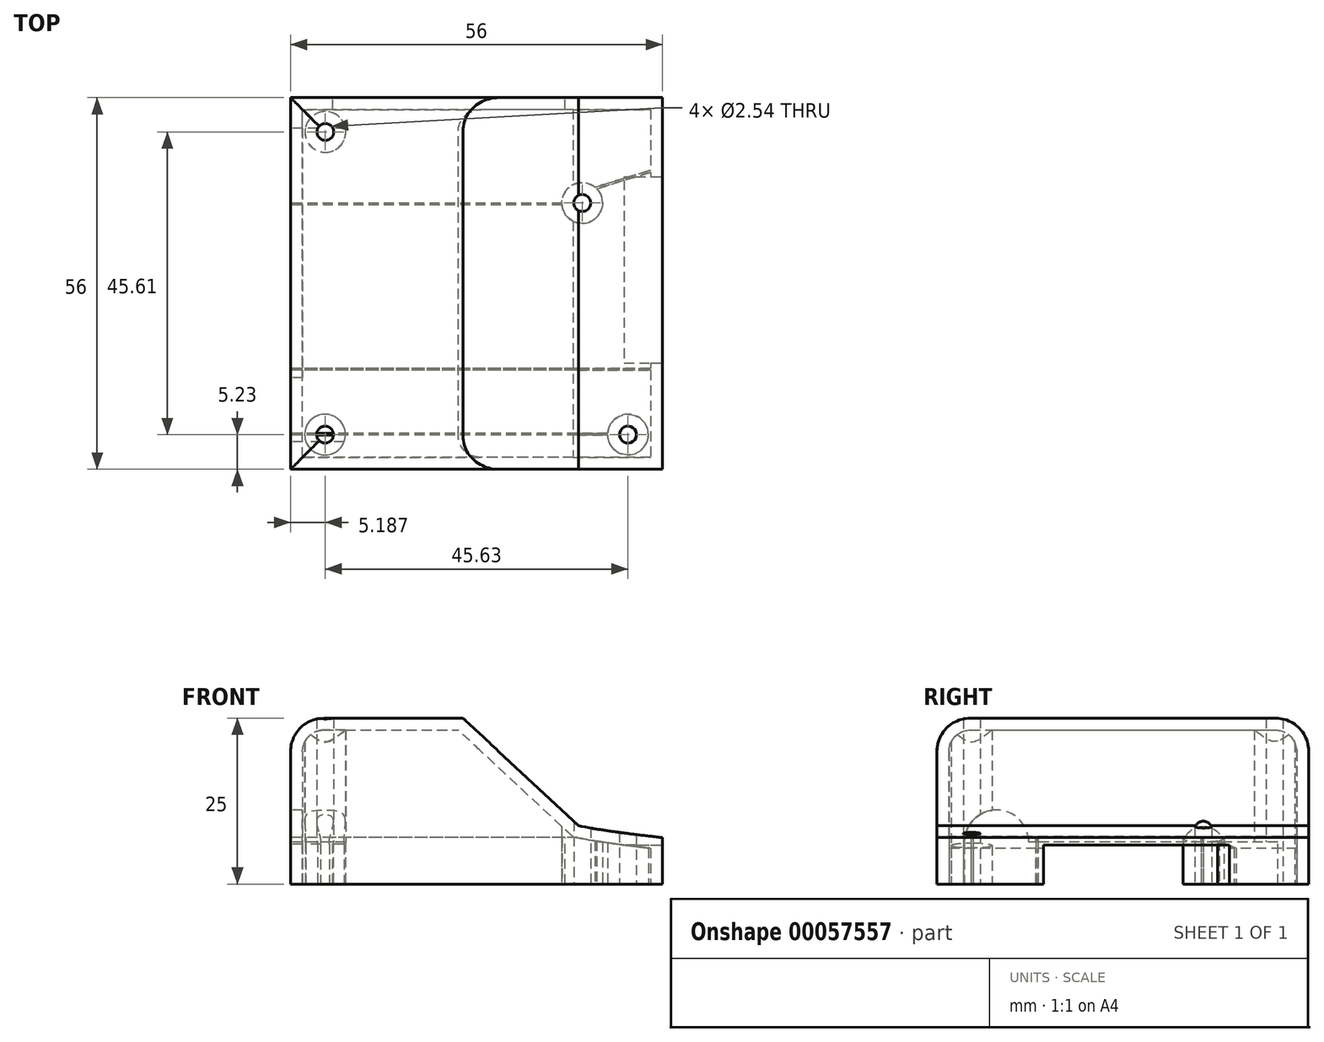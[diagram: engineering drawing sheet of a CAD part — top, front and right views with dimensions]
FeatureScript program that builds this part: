
annotation { "Feature Type Name" : "Feature", "Feature Type Description" : "" }
export const myFeature = defineFeature(function(context is Context, id is Id, definition is map)
    precondition{}
    {
        {
            var Q0;
            Q0=qCreatedBy(makeId("Top.planeOp"),FACE);
            var sketch = newSketch(context, id + "F0", { "sketchPlane" : qUnion([Q0])});
            skLineSegment(sketch, "E0.rect.bottom", {"start": v(22.84, -21.13) * mm, "end": v(-26.83, -21.13) * mm});
            skLineSegment(sketch, "E0.rect.top", {"start": v(22.84, 28.7) * mm, "end": v(-26.83, 28.7) * mm});
            skLineSegment(sketch, "E0.rect.left", {"start": v(22.84, -21.13) * mm, "end": v(22.84, 28.7) * mm});
            skPoint(sketch, "E0.rect.middle", {"position": v(-2, 3.78) * mm});
            skCircle(sketch, "E1", {"center": v(-24.81, -18.99) * mm, "radius": 1.27 * mm});
            skCircle(sketch, "E2", {"center": v(-24.76, 26.62) * mm, "radius": 1.27 * mm});
            skCircle(sketch, "E3", {"center": v(13.92, 15.91) * mm, "radius": 1.27 * mm});
            skLineSegment(sketch, "E4", {"start": v(-2, -21.13) * mm, "end": v(-2, -18.21) * mm});
            skCircle(sketch, "E5.MirrorC", {"center": v(20.82, -18.99) * mm, "radius": 1.27 * mm});
            skLineSegment(sketch, "E6.rect.bottom", {"start": v(24.75, -22.97) * mm, "end": v(-28.75, -22.97) * mm});
            skLineSegment(sketch, "E6.rect.top", {"start": v(24.75, 30.53) * mm, "end": v(-28.75, 30.53) * mm});
            skLineSegment(sketch, "E6.rect.left", {"start": v(24.75, -22.97) * mm, "end": v(24.75, 30.53) * mm});
            skLineSegment(sketch, "E6.rect.right", {"start": v(-28.75, -22.97) * mm, "end": v(-28.75, 30.53) * mm});
            skLineSegment(sketch, "E7.rect.bottom", {"start": v(26, -24.22) * mm, "end": v(-30, -24.22) * mm});
            skLineSegment(sketch, "E7.rect.top", {"start": v(26, 31.78) * mm, "end": v(-30, 31.78) * mm});
            skLineSegment(sketch, "E7.rect.left", {"start": v(26, -24.22) * mm, "end": v(26, 31.78) * mm});
            skLineSegment(sketch, "E7.rect.right", {"start": v(-30, -24.22) * mm, "end": v(-30, 31.78) * mm});
            skPoint(sketch, "E8", {"position": v(8.65, 14) * mm});
            skSolve(sketch);
        }
        {
            var Q0;
            Q0 = qSketchRegion(id + "F0", true);
            var Q1;
            Q1=makeQuery(id+"F0.imprint","IMPRINT",FACE,{"disambiguationData":[TD([[makeQuery(id+"F0.imprint","IMPRINT",EDGE,{"derivedFrom":sQuery(id+"F0.wireOp",EDGE,"E1")}),-1.0]])]});
            extrude(context, id + "F1", {"entities" : qUnion([Q0, Q1]), "depth" : 25 * mm});
        }
        {
            var Q0;
            Q0=qCreatedBy(makeId("Front.planeOp"),FACE);
            var sketch = newSketch(context, id + "F2", { "sketchPlane" : qUnion([Q0])});
            skLineSegment(sketch, "E9", {"start": v(0, 0) * mm, "end": v(0, 7) * mm});
            skLineSegment(sketch, "E10", {"start": v(0, 7) * mm, "end": v(26.03, 7) * mm});
            skFitSpline(sketch, "E11", {"points": [v(26.03, 7) * mm, v(0, 12.35) * mm, v(-16.78, 25.51) * mm], "startDerivative": vector(-52.99, 5.48) * mm, "endDerivative": vector(-32.25, 32.04) * mm});
            skLineSegment(sketch, "E12", {"start": v(26.03, 7) * mm, "end": v(26.03, 25.51) * mm});
            skLineSegment(sketch, "E13", {"start": v(26.03, 25.51) * mm, "end": v(-16.78, 25.51) * mm});
            skFitSpline(sketch, "E14", {"points": [v(26.03, 7) * mm, v(6, 12.87) * mm, v(0, 25.51) * mm], "startDerivative": vector(-42.79, 5.9) * mm, "endDerivative": vector(-8.1, 32) * mm});
            skFitSpline(sketch, "E15", {"points": [v(26.03, 7) * mm, v(2.41, 13.05) * mm, v(-4.6, 25.51) * mm], "startDerivative": vector(-48.93, 5.58) * mm, "endDerivative": vector(-10.6, 32.65) * mm});
            skLineSegment(sketch, "E16", {"start": v(-4.6, 25.51) * mm, "end": v(15.3, 7) * mm});
            skLineSegment(sketch, "E17", {"start": v(15.3, 7) * mm, "end": v(26.03, 7) * mm});
            skSolve(sketch);
        }
        {
            var Q0;
            {var subQ0=sQuery(id+"F2.wireOp",EDGE,"E14");Q0=makeQuery(id+"F2.imprint","IMPRINT",FACE,{"disambiguationData":[TD([[makeQuery(id+"F2.imprint","IMPRINT",EDGE,{"derivedFrom":subQ0}),1.0]])]});}
            var Q1;
            {var subQ0=sQuery(id+"F2.wireOp",EDGE,"E12");Q1=makeQuery(id+"F2.imprint","IMPRINT",FACE,{"disambiguationData":[TD([[makeQuery(id+"F2.imprint","IMPRINT",EDGE,{"derivedFrom":subQ0}),1.0]])]});}
            extrude(context, id + "F3", {"entities" : qUnion([Q0, Q1]), "operationType" : NewBodyOperationType.REMOVE, "endBound" : BoundingType.UP_TO_NEXT, "oppositeDirection" : true, "depth" : 25 * mm, "hasSecondDirection" : true, "secondDirectionOppositeDirection" : false, "secondDirectionDepth" : 25 * mm});
        }
        {
            var Q0;
            Q0=makeQuery(id+"F1.opExtrude","CAP_EDGE",EDGE,{"disambiguationData":[OSD([sQuery(id+"F0.wireOp",EDGE,"E7.rect.right")])],"isStart":false});
            var Q1;
            Q1=makeQuery(id+"F3.boolean.opBoolean","COPY",EDGE,{"derivedFrom":makeQuery(id+"F3.opExtrude","TWEAK_EDGE",EDGE,{"derivedFrom":[makeQuery(id+"F1.opExtrude","CAP_FACE",FACE,{"disambiguationData":[OSD([sQuery(id+"F0.wireOp",EDGE,"E1"),sQuery(id+"F0.wireOp",EDGE,"E2"),sQuery(id+"F0.wireOp",EDGE,"E3"),sQuery(id+"F0.wireOp",EDGE,"E5.MirrorC"),sQuery(id+"F0.wireOp",EDGE,"E7.rect.bottom"),sQuery(id+"F0.wireOp",EDGE,"E7.rect.top"),sQuery(id+"F0.wireOp",EDGE,"E7.rect.left"),sQuery(id+"F0.wireOp",EDGE,"E7.rect.right")])],"isStart":false}),makeQuery(id+"F2.imprint","IMPRINT",EDGE,{"derivedFrom":sQuery(id+"F2.wireOp",EDGE,"E11")})]})});
            var Q2;
            Q2=makeQuery(id+"F3.boolean.opBoolean","COPY",EDGE,{"derivedFrom":makeQuery(id+"F3.opExtrude","TWEAK_EDGE",EDGE,{"derivedFrom":[makeQuery(id+"F1.opExtrude","CAP_FACE",FACE,{"disambiguationData":[OSD([sQuery(id+"F0.wireOp",EDGE,"E1"),sQuery(id+"F0.wireOp",EDGE,"E2"),sQuery(id+"F0.wireOp",EDGE,"E3"),sQuery(id+"F0.wireOp",EDGE,"E5.MirrorC"),sQuery(id+"F0.wireOp",EDGE,"E7.rect.bottom"),sQuery(id+"F0.wireOp",EDGE,"E7.rect.top"),sQuery(id+"F0.wireOp",EDGE,"E7.rect.left"),sQuery(id+"F0.wireOp",EDGE,"E7.rect.right")])],"isStart":false}),makeQuery(id+"F2.imprint","IMPRINT",EDGE,{"derivedFrom":sQuery(id+"F2.wireOp",EDGE,"E15")})]})});
            var Q3;
            Q3=makeQuery(id+"F3.boolean.opBoolean","COPY",EDGE,{"derivedFrom":makeQuery(id+"F3.opExtrude","CAP_EDGE",EDGE,{"disambiguationData":[OSD([sQuery(id+"F2.wireOp",EDGE,"E16")]),topologyDisambiguationEdgeConnected([makeQuery(id+"F1.opExtrude","CAP_FACE",FACE,{"disambiguationData":[OSD([sQuery(id+"F0.wireOp",EDGE,"E1"),sQuery(id+"F0.wireOp",EDGE,"E2"),sQuery(id+"F0.wireOp",EDGE,"E3"),sQuery(id+"F0.wireOp",EDGE,"E5.MirrorC"),sQuery(id+"F0.wireOp",EDGE,"E7.rect.bottom"),sQuery(id+"F0.wireOp",EDGE,"E7.rect.top"),sQuery(id+"F0.wireOp",EDGE,"E7.rect.left"),sQuery(id+"F0.wireOp",EDGE,"E7.rect.right")])],"isStart":false})])],"isStart":false})});
            var Q4;
            {var subQ0=sQuery(id+"F2.wireOp",EDGE,"E16");var subQ1=sQuery(id+"F2.wireOp",EDGE,"E14");var subQ2=makeQuery(id+"F2.imprint","INTERSECT",VERTEX,{"disambiguationData":[OD(0.0)],"derivedFrom":[subQ1,subQ0]});var subQ3=sQuery(id+"F2.wireOp",EDGE,"E15");var subQ4=makeQuery(id+"F2.imprint","INTERSECT",VERTEX,{"derivedFrom":[subQ3,subQ0]});var subQ5=makeQuery(id+"F2.imprint","INTERSECT",VERTEX,{"disambiguationData":[OD(1.0)],"derivedFrom":[subQ1,subQ0]});Q4=makeQuery(id+"F3.boolean.opBoolean","COPY",EDGE,{"derivedFrom":makeQuery(id+"F3.opExtrude","TWEAK_EDGE",EDGE,{"disambiguationData":[OD(0.0)],"derivedFrom":[makeQuery(id+"F2.imprint","IMPRINT",EDGE,{"disambiguationData":[TD([[subQ4,1.0]])],"derivedFrom":subQ3}),makeQuery(id+"F2.imprint","IMPRINT",EDGE,{"disambiguationData":[TD([[subQ5,1.0]])],"derivedFrom":subQ0}),makeQuery(id+"F2.imprint","IMPRINT",EDGE,{"disambiguationData":[TD([[subQ2,1.0]])],"derivedFrom":subQ0}),makeQuery(id+"F2.imprint","IMPRINT",EDGE,{"disambiguationData":[TD([[subQ2,-1.0]])],"derivedFrom":subQ0})]})});}
            var Q5;
            {var subQ0=sQuery(id+"F2.wireOp",EDGE,"E16");var subQ1=sQuery(id+"F2.wireOp",EDGE,"E14");var subQ2=makeQuery(id+"F2.imprint","INTERSECT",VERTEX,{"disambiguationData":[OD(0.0)],"derivedFrom":[subQ1,subQ0]});var subQ3=sQuery(id+"F2.wireOp",EDGE,"E15");var subQ4=makeQuery(id+"F2.imprint","INTERSECT",VERTEX,{"derivedFrom":[subQ3,subQ0]});var subQ5=makeQuery(id+"F2.imprint","INTERSECT",VERTEX,{"disambiguationData":[OD(1.0)],"derivedFrom":[subQ1,subQ0]});Q5=makeQuery(id+"F3.boolean.opBoolean","COPY",EDGE,{"derivedFrom":makeQuery(id+"F3.opExtrude","TWEAK_EDGE",EDGE,{"disambiguationData":[OD(1.0)],"derivedFrom":[makeQuery(id+"F2.imprint","IMPRINT",EDGE,{"disambiguationData":[TD([[subQ4,1.0]])],"derivedFrom":subQ3}),makeQuery(id+"F2.imprint","IMPRINT",EDGE,{"disambiguationData":[TD([[subQ5,1.0]])],"derivedFrom":subQ0}),makeQuery(id+"F2.imprint","IMPRINT",EDGE,{"disambiguationData":[TD([[subQ2,1.0]])],"derivedFrom":subQ0}),makeQuery(id+"F2.imprint","IMPRINT",EDGE,{"disambiguationData":[TD([[subQ2,-1.0]])],"derivedFrom":subQ0})]})});}
            var Q6;
            Q6=makeQuery(id+"F1.opExtrude","CAP_EDGE",EDGE,{"disambiguationData":[OSD([sQuery(id+"F0.wireOp",EDGE,"E7.rect.bottom")])],"isStart":false});
            var Q7;
            Q7=makeQuery(id+"F3.boolean.opBoolean","COPY",EDGE,{"derivedFrom":makeQuery(id+"F3.opExtrude","CAP_EDGE",EDGE,{"disambiguationData":[OSD([sQuery(id+"F2.wireOp",EDGE,"E16")])],"isStart":true})});
            var Q8;
            Q8=makeQuery(id+"F1.opExtrude","CAP_EDGE",EDGE,{"disambiguationData":[OSD([sQuery(id+"F0.wireOp",EDGE,"E7.rect.top")])],"isStart":false});
            var Q9;
            Q9=makeQuery(id+"F3.boolean.opBoolean","COPY",EDGE,{"derivedFrom":makeQuery(id+"F3.opExtrude","CAP_EDGE",EDGE,{"disambiguationData":[OSD([sQuery(id+"F2.wireOp",EDGE,"E16")]),topologyDisambiguationEdgeConnected([makeQuery(id+"F1.opExtrude","SWEPT_FACE",FACE,{"disambiguationData":[OSD([sQuery(id+"F0.wireOp",EDGE,"E7.rect.top")])]})])],"isStart":false})});
            fillet(context, id + "F4", {"entities" : qUnion([Q0, Q1, Q2, Q3, Q4, Q5, Q6, Q7, Q8, Q9]), "radius" : 5 * mm, "tangentPropagation" : true, "allowEdgeOverflow" : false});
        }
        {
            var Q0;
            Q0=makeQuery(id+"F1.opExtrude","SWEPT_BODY",BODY,{"disambiguationData":[OSD([sQuery(id+"F0.wireOp",EDGE,"E1"),sQuery(id+"F0.wireOp",EDGE,"E2"),sQuery(id+"F0.wireOp",EDGE,"E3"),sQuery(id+"F0.wireOp",EDGE,"E5.MirrorC"),sQuery(id+"F0.wireOp",EDGE,"E7.rect.bottom"),sQuery(id+"F0.wireOp",EDGE,"E7.rect.top"),sQuery(id+"F0.wireOp",EDGE,"E7.rect.left"),sQuery(id+"F0.wireOp",EDGE,"E7.rect.right")])]});
            transform(context, id + "F5", {"entities" : qUnion([Q0]), "transformType" : TransformType.TRANSLATION_3D, "dx" : -5 * mm, "dy" : -12 * mm, "dz" : 0 * mm, "makeCopy" : false});
        }
        {
            var Q0;
            Q0=makeQuery(id+"F1.opExtrude","CAP_FACE",FACE,{"disambiguationData":[OSD([sQuery(id+"F0.wireOp",EDGE,"E1"),sQuery(id+"F0.wireOp",EDGE,"E2"),sQuery(id+"F0.wireOp",EDGE,"E3"),sQuery(id+"F0.wireOp",EDGE,"E5.MirrorC"),sQuery(id+"F0.wireOp",EDGE,"E7.rect.bottom"),sQuery(id+"F0.wireOp",EDGE,"E7.rect.top"),sQuery(id+"F0.wireOp",EDGE,"E7.rect.left"),sQuery(id+"F0.wireOp",EDGE,"E7.rect.right")])],"isStart":true});
            shell(context, id + "F6", {"entities" : qUnion([Q0]), "thickness" : 1.8 * mm});
        }
        {
            var Q0;
            Q0=makeQuery(id+"F1.opExtrude","SWEPT_FACE",FACE,{"disambiguationData":[OSD([sQuery(id+"F0.wireOp",EDGE,"E7.rect.left")])]});
            cPlane(context, id + "F7", {"entities" : qUnion([Q0]), "cplaneType" : CPlaneType.OFFSET, "offset" : 0 * mm, "width" : 150 * mm, "height" : 150 * mm});
        }
        {
            var Q0;
            Q0=qCreatedBy(id+"F7.planeOp",FACE);
            var sketch = newSketch(context, id + "F8", { "sketchPlane" : qUnion([Q0])});
            skLineSegment(sketch, "E18.bottom", {"start": v(7.84, 0) * mm, "end": v(-20.2, 0) * mm});
            skLineSegment(sketch, "E18.top", {"start": v(7.84, 5.87) * mm, "end": v(-20.2, 5.87) * mm});
            skLineSegment(sketch, "E18.left", {"start": v(7.84, 0) * mm, "end": v(7.84, 5.87) * mm});
            skLineSegment(sketch, "E18.right", {"start": v(-20.2, 0) * mm, "end": v(-20.2, 5.87) * mm});
            skSolve(sketch);
        }
        {
            var Q0;
            Q0 = qSketchRegion(id + "F8", true);
            extrude(context, id + "F9", {"entities" : qUnion([Q0]), "operationType" : NewBodyOperationType.REMOVE, "endBound" : BoundingType.UP_TO_NEXT, "oppositeDirection" : true, "depth" : 25 * mm});
        }
        {
            var Q0;
            Q0=makeQuery(id+"F1.opExtrude","SWEPT_FACE",FACE,{"disambiguationData":[OSD([sQuery(id+"F0.wireOp",EDGE,"E7.rect.right")])]});
            cPlane(context, id + "F10", {"entities" : qUnion([Q0]), "cplaneType" : CPlaneType.OFFSET, "offset" : 0 * mm, "width" : 150 * mm, "height" : 150 * mm});
        }
        {
            var Q0;
            Q0=qCreatedBy(id+"F10.planeOp",FACE);
            var sketch = newSketch(context, id + "F11", { "sketchPlane" : qUnion([Q0])});
            skLineSegment(sketch, "E19.bottom", {"start": v(-15.15, 0) * mm, "end": v(22.4, 0) * mm});
            skLineSegment(sketch, "E19.top", {"start": v(-15.15, 6.31) * mm, "end": v(22.4, 6.31) * mm});
            skLineSegment(sketch, "E19.left", {"start": v(-15.15, 0) * mm, "end": v(-15.15, 6.31) * mm});
            skArc(sketch, "E20", {"start": v(32.08, 6) * mm, "mid": v(27.4, 11.15) * mm, "end": v(22.4, 6.31) * mm});
            skLineSegment(sketch, "E21", {"start": v(32.08, 6.63) * mm, "end": v(32.08, 0) * mm});
            skLineSegment(sketch, "E22", {"start": v(32.08, 0) * mm, "end": v(22.4, 0) * mm});
            skSolve(sketch);
        }
        {
            var Q0;
            Q0 = qSketchRegion(id + "F11", true);
            extrude(context, id + "F12", {"entities" : qUnion([Q0]), "operationType" : NewBodyOperationType.REMOVE, "oppositeDirection" : true, "depth" : 25 * mm});
        }
        {
            var Q0;
            Q0=makeQuery(id+"F1.opExtrude","SWEPT_FACE",FACE,{"disambiguationData":[OSD([sQuery(id+"F0.wireOp",EDGE,"E7.rect.top")])]});
            cPlane(context, id + "F13", {"entities" : qUnion([Q0]), "cplaneType" : CPlaneType.OFFSET, "offset" : 0 * mm, "width" : 150 * mm, "height" : 150 * mm});
        }
        {
            var Q0;
            Q0=qCreatedBy(id+"F13.planeOp",FACE);
            var sketch = newSketch(context, id + "F14", { "sketchPlane" : qUnion([Q0])});
            skLineSegment(sketch, "E23.bottom", {"start": v(-6.36, 0) * mm, "end": v(28.67, 0) * mm});
            skLineSegment(sketch, "E23.top", {"start": v(-6.36, 7.05) * mm, "end": v(28.67, 7.05) * mm});
            skLineSegment(sketch, "E23.left", {"start": v(-6.36, 0) * mm, "end": v(-6.36, 7.05) * mm});
            skLineSegment(sketch, "E23.right", {"start": v(28.67, 0) * mm, "end": v(28.67, 7.05) * mm});
            skSolve(sketch);
        }
        {
            var Q0;
            Q0 = qSketchRegion(id + "F14", true);
            extrude(context, id + "F15", {"entities" : qUnion([Q0]), "operationType" : NewBodyOperationType.REMOVE, "endBound" : BoundingType.UP_TO_NEXT, "oppositeDirection" : true, "depth" : 25 * mm});
        }
        {
            var Q0;
            Q0=qCreatedBy(makeId("Top.planeOp"),FACE);
            var sketch = newSketch(context, id + "F16", { "sketchPlane" : qUnion([Q0])});
            skLineSegment(sketch, "E24", {"start": v(12.81, -31.08) * mm, "end": v(12.81, -30.78) * mm});
            skLineSegment(sketch, "E25", {"start": v(19.24, -20.99) * mm, "end": v(19.24, -21.29) * mm});
            skLineSegment(sketch, "E26", {"start": v(19.24, 8.54) * mm, "end": v(19.24, 8.84) * mm});
            skLineSegment(sketch, "E27", {"start": v(5.94, 3.59) * mm, "end": v(5.94, 3.89) * mm});
            skLineSegment(sketch, "E28", {"start": v(10.65, 6.22) * mm, "end": v(10.65, 5.92) * mm});
            skLineSegment(sketch, "E29", {"start": v(10.65, 6.22) * mm, "end": v(19.24, 8.84) * mm});
            skLineSegment(sketch, "E30", {"start": v(10.65, 5.92) * mm, "end": v(19.24, 8.54) * mm});
            skLineSegment(sketch, "E31", {"start": v(19.24, -21.29) * mm, "end": v(-34.98, -21.29) * mm});
            skLineSegment(sketch, "E32", {"start": v(19.24, -20.99) * mm, "end": v(-34.98, -20.99) * mm});
            skLineSegment(sketch, "E33", {"start": v(-34.98, -20.99) * mm, "end": v(-34.98, -21.29) * mm});
            skLineSegment(sketch, "E34", {"start": v(12.81, -31.08) * mm, "end": v(-34.98, -31.08) * mm});
            skLineSegment(sketch, "E35", {"start": v(12.81, -30.78) * mm, "end": v(-34.98, -30.78) * mm});
            skLineSegment(sketch, "E36", {"start": v(-34.98, -30.78) * mm, "end": v(-34.98, -31.08) * mm});
            skLineSegment(sketch, "E37", {"start": v(5.94, 3.59) * mm, "end": v(-34.95, 3.59) * mm});
            skLineSegment(sketch, "E38", {"start": v(5.94, 3.89) * mm, "end": v(-34.95, 3.89) * mm});
            skLineSegment(sketch, "E39", {"start": v(-34.95, 3.89) * mm, "end": v(-34.95, 3.59) * mm});
            skSolve(sketch);
        }
        {
            var Q0;
            Q0 = qSketchRegion(id + "F16", true);
            extrude(context, id + "F17", {"entities" : qUnion([Q0]), "operationType" : NewBodyOperationType.ADD, "depth" : 7 * mm});
        }
    });
